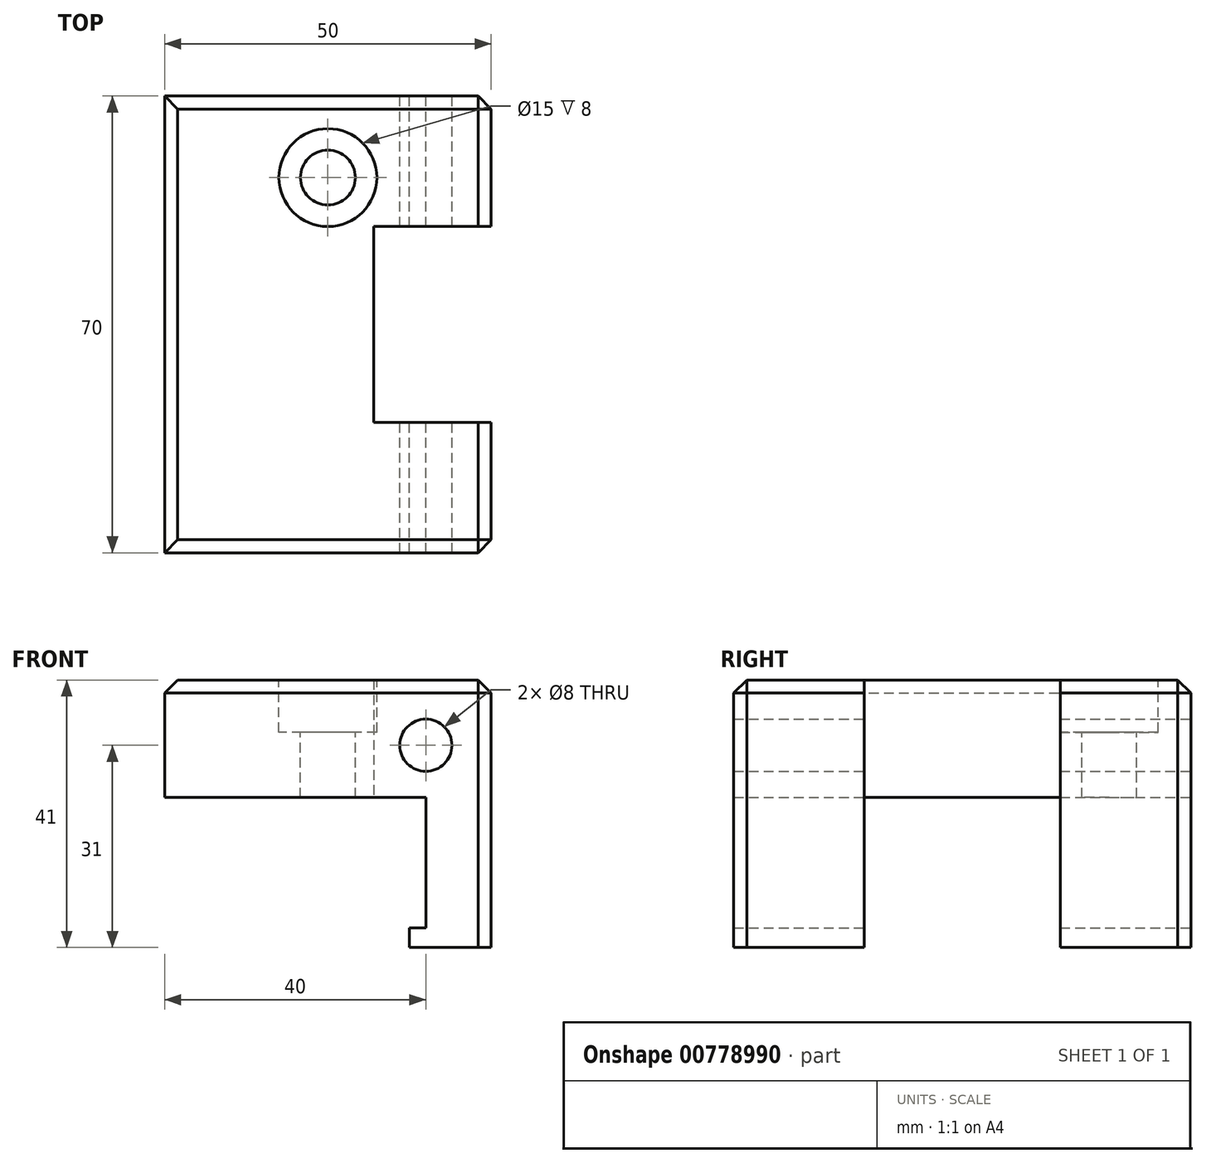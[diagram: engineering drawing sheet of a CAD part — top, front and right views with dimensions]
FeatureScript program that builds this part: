
annotation { "Feature Type Name" : "Feature", "Feature Type Description" : "" }
export const myFeature = defineFeature(function(context is Context, id is Id, definition is map)
    precondition{}
    {
        {
            var Q0;
            Q0=qCreatedBy(makeId("Front.planeOp"),FACE);
            var sketch = newSketch(context, id + "F0", { "sketchPlane" : qUnion([Q0])});
            skLineSegment(sketch, "E0", {"start": v(0, 0) * mm, "end": v(-40, 0) * mm});
            skLineSegment(sketch, "E1", {"start": v(-40, 0) * mm, "end": v(-40, 18) * mm});
            skLineSegment(sketch, "E2", {"start": v(-40, 18) * mm, "end": v(10, 18) * mm});
            skLineSegment(sketch, "E3", {"start": v(10, 18) * mm, "end": v(10, -23) * mm});
            skLineSegment(sketch, "E4", {"start": v(10, -23) * mm, "end": v(-2.5, -23) * mm});
            skLineSegment(sketch, "E5", {"start": v(-2.5, -23) * mm, "end": v(-2.5, -20) * mm});
            skLineSegment(sketch, "E6", {"start": v(-2.5, -20) * mm, "end": v(0, -20) * mm});
            skLineSegment(sketch, "E7", {"start": v(0, -20) * mm, "end": v(0, 0) * mm});
            skCircle(sketch, "E8", {"center": v(0, 8) * mm, "radius": 4 * mm});
            skSolve(sketch);
        }
        {
            var Q0;
            Q0=makeQuery(id+"F0.imprint","IMPRINT",FACE,{"disambiguationData":[TD([[makeQuery(id+"F0.imprint","IMPRINT",EDGE,{"derivedFrom":sQuery(id+"F0.wireOp",EDGE,"E0")}),-1.0]])]});
            extrude(context, id + "F1", {"entities" : qUnion([Q0]), "endBound" : BoundingType.SYMMETRIC, "depth" : 70 * mm, "offsetDistance" : 25 * mm});
        }
        {
            var Q0;
            Q0=qCreatedBy(makeId("Front.planeOp"),FACE);
            var sketch = newSketch(context, id + "F2", { "sketchPlane" : qUnion([Q0])});
            skLineSegment(sketch, "E9.bottom", {"start": v(10, 18) * mm, "end": v(-8, 18) * mm});
            skLineSegment(sketch, "E9.top", {"start": v(10, -23) * mm, "end": v(-8, -23) * mm});
            skLineSegment(sketch, "E9.left", {"start": v(10, 18) * mm, "end": v(10, -23) * mm});
            skLineSegment(sketch, "E9.right", {"start": v(-8, 18) * mm, "end": v(-8, -23) * mm});
            skSolve(sketch);
        }
        {
            var Q0;
            Q0=makeQuery(id+"F1.opExtrude","SWEPT_EDGE",EDGE,{"disambiguationData":[OSD([sQuery(id+"F0.wireOp",EDGE,"E2"),sQuery(id+"F0.wireOp",EDGE,"E3")])]});
            var Q1;
            Q1=makeQuery(id+"F1.opExtrude","CAP_EDGE",EDGE,{"disambiguationData":[OSD([sQuery(id+"F0.wireOp",EDGE,"E3")])],"isStart":false});
            var Q2;
            Q2=makeQuery(id+"F1.opExtrude","CAP_EDGE",EDGE,{"disambiguationData":[OSD([sQuery(id+"F0.wireOp",EDGE,"E3")])],"isStart":true});
            var Q3;
            Q3=makeQuery(id+"F1.opExtrude","CAP_EDGE",EDGE,{"disambiguationData":[OSD([sQuery(id+"F0.wireOp",EDGE,"E2")])],"isStart":true});
            var Q4;
            Q4=makeQuery(id+"F1.opExtrude","CAP_EDGE",EDGE,{"disambiguationData":[OSD([sQuery(id+"F0.wireOp",EDGE,"E2")])],"isStart":false});
            var Q5;
            Q5=makeQuery(id+"F1.opExtrude","SWEPT_EDGE",EDGE,{"disambiguationData":[OSD([sQuery(id+"F0.wireOp",EDGE,"E1"),sQuery(id+"F0.wireOp",EDGE,"E2")])]});
            chamfer(context, id + "F3", {"entities" : qUnion([Q0, Q1, Q2, Q3, Q4, Q5]), "width" : 2 * mm, "tangentPropagation" : true});
        }
        {
            var Q0;
            Q0 = qSketchRegion(id + "F2", true);
            extrude(context, id + "F4", {"entities" : qUnion([Q0]), "operationType" : NewBodyOperationType.REMOVE, "endBound" : BoundingType.SYMMETRIC, "oppositeDirection" : true, "depth" : 30 * mm, "offsetDistance" : 25 * mm});
        }
        {
            var Q0;
            Q0=makeQuery(id+"F1.opExtrude","SWEPT_FACE",FACE,{"disambiguationData":[OSD([sQuery(id+"F0.wireOp",EDGE,"E2")])]});
            var sketch = newSketch(context, id + "F5", { "sketchPlane" : qUnion([Q0])});
            skPoint(sketch, "E10", {"position": v(-15, 22.5) * mm});
            skSolve(sketch);
        }
        {
            var Q0;
            Q0=sQuery(id+"F5.wireOp",VERTEX,"E10");
            var Q1;
            Q1=makeQuery(id+"F1.opExtrude","SWEPT_BODY",BODY,{"disambiguationData":[OSD([sQuery(id+"F0.wireOp",EDGE,"E0"),sQuery(id+"F0.wireOp",EDGE,"E1"),sQuery(id+"F0.wireOp",EDGE,"E2"),sQuery(id+"F0.wireOp",EDGE,"E3"),sQuery(id+"F0.wireOp",EDGE,"E4"),sQuery(id+"F0.wireOp",EDGE,"E5"),sQuery(id+"F0.wireOp",EDGE,"E6"),sQuery(id+"F0.wireOp",EDGE,"E7"),sQuery(id+"F0.wireOp",EDGE,"E8")])]});
            hole(context, id + "F6", {"style" : HoleStyle.C_BORE, "endStyle" : HoleEndStyle.THROUGH, "holeDiameter" : 8.4 * mm, "cBoreDiameter" : 15 * mm, "cBoreDepth" : 8 * mm, "majorDiameter" : 12 * mm, "tappedDepth" : 10.75 * mm, "tapClearance" : 3, "startFromSketch" : true, "locations" : qUnion([Q0]), "scope" : qUnion([Q1])});
        }
    });
